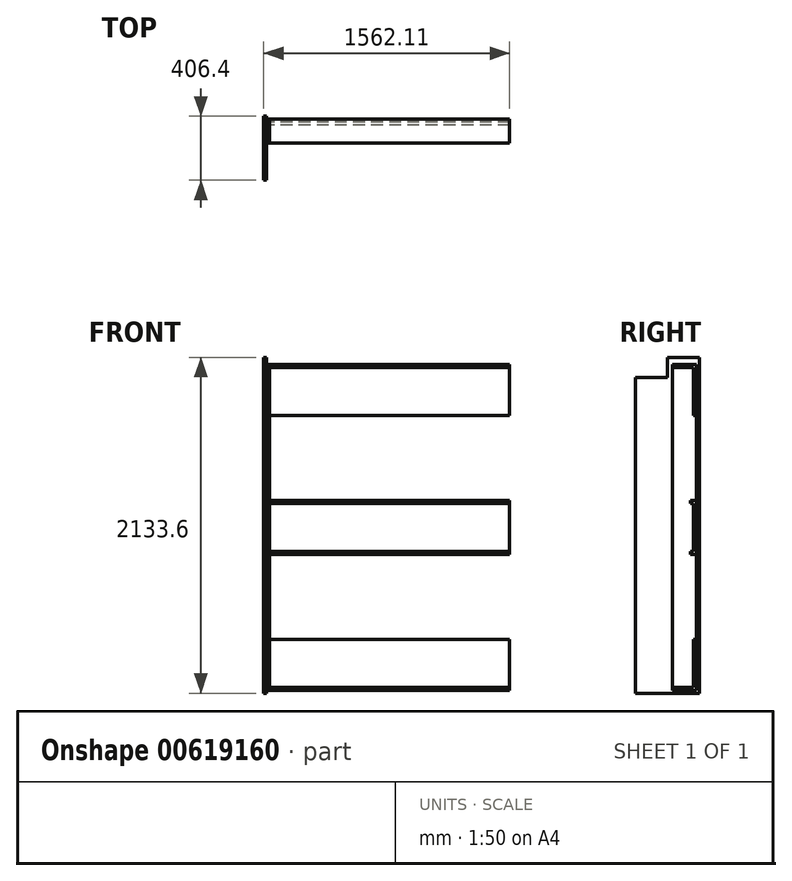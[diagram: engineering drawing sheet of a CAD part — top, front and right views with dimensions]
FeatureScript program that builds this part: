
annotation { "Feature Type Name" : "Feature", "Feature Type Description" : "" }
export const myFeature = defineFeature(function(context is Context, id is Id, definition is map)
    precondition{}
    {
        {
            var Q0;
            Q0=qCreatedBy(makeId("Right.planeOp"),FACE);
            var sketch = newSketch(context, id + "F0", { "sketchPlane" : qUnion([Q0])});
            skLineSegment(sketch, "E0.bottom", {"start": v(0, 0) * mm, "end": v(-406.4, 0) * mm});
            skLineSegment(sketch, "E0.top", {"start": v(0, 2133.6) * mm, "end": v(-203.2, 2133.6) * mm});
            skLineSegment(sketch, "E0.left", {"start": v(0, 0) * mm, "end": v(0, 2133.6) * mm});
            skLineSegment(sketch, "E0.right", {"start": v(-406.4, 0) * mm, "end": v(-406.4, 2006.6) * mm});
            skLineSegment(sketch, "E1", {"start": v(-203.2, 2133.6) * mm, "end": v(-203.2, 2006.6) * mm});
            skLineSegment(sketch, "E2", {"start": v(-203.2, 2006.6) * mm, "end": v(-406.4, 2006.6) * mm});
            skSolve(sketch);
        }
        {
            var Q0;
            Q0=makeQuery(id+"F0.imprint","IMPRINT",FACE,{"disambiguationData":[TD([[makeQuery(id+"F0.imprint","IMPRINT",EDGE,{"derivedFrom":sQuery(id+"F0.wireOp",EDGE,"E0.bottom")}),-1.0]])]});
            extrude(context, id + "F1", {"entities" : qUnion([Q0]), "depth" : 19.05 * mm, "offsetDistance" : 25.4 * mm});
        }
        {
            var Q0;
            Q0=makeQuery(id+"F1.opExtrude","CAP_FACE",FACE,{"disambiguationData":[OSD([sQuery(id+"F0.wireOp",EDGE,"E0.bottom"),sQuery(id+"F0.wireOp",EDGE,"E0.top"),sQuery(id+"F0.wireOp",EDGE,"E0.left"),sQuery(id+"F0.wireOp",EDGE,"E0.right"),sQuery(id+"F0.wireOp",EDGE,"E1"),sQuery(id+"F0.wireOp",EDGE,"E2")])],"isStart":false});
            cPlane(context, id + "F2", {"entities" : qUnion([Q0]), "cplaneType" : CPlaneType.OFFSET, "offset" : 3 / 406.4 * mm, "width" : 152.4 * mm, "height" : 152.4 * mm});
        }
        {
            var Q0;
            Q0=qCreatedBy(id+"F2.planeOp",FACE);
            var sketch = newSketch(context, id + "F3", { "sketchPlane" : qUnion([Q0])});
            skLineSegment(sketch, "E3.bottom", {"start": v(-19.05, 38.1) * mm, "end": v(-171.45, 38.1) * mm});
            skLineSegment(sketch, "E3.top", {"start": v(-19.05, 2070.1) * mm, "end": v(-171.45, 2070.1) * mm});
            skLineSegment(sketch, "E3.left", {"start": v(-19.05, 38.1) * mm, "end": v(-19.05, 2070.1) * mm});
            skLineSegment(sketch, "E3.right", {"start": v(-171.45, 38.1) * mm, "end": v(-171.45, 2070.1) * mm});
            skLineSegment(sketch, "E4.top", {"start": v(-19.05, 2089.15) * mm, "end": v(-171.45, 2089.15) * mm});
            skLineSegment(sketch, "E4.left", {"start": v(-19.05, 2070.1) * mm, "end": v(-19.05, 2089.15) * mm});
            skLineSegment(sketch, "E4.right", {"start": v(-171.45, 2070.1) * mm, "end": v(-171.45, 2089.15) * mm});
            skLineSegment(sketch, "E5.top", {"start": v(-19.05, 19.05) * mm, "end": v(-171.45, 19.05) * mm});
            skLineSegment(sketch, "E5.left", {"start": v(-19.05, 38.1) * mm, "end": v(-19.05, 19.05) * mm});
            skLineSegment(sketch, "E5.right", {"start": v(-171.45, 38.1) * mm, "end": v(-171.45, 19.05) * mm});
            skSolve(sketch);
        }
        {
            var Q0;
            Q0 = qSketchRegion(id + "F3", true);
            extrude(context, id + "F4", {"entities" : qUnion([Q0]), "depth" : 19.05 * mm, "offsetDistance" : 25.4 * mm});
        }
        {
            var Q0;
            Q0=makeQuery(id+"F4.opExtrude","CAP_FACE",FACE,{"disambiguationData":[OSD([sQuery(id+"F3.wireOp",EDGE,"E3.bottom"),sQuery(id+"F3.wireOp",EDGE,"E3.top"),sQuery(id+"F3.wireOp",EDGE,"E3.left"),sQuery(id+"F3.wireOp",EDGE,"E3.right")])],"isStart":false});
            var sketch = newSketch(context, id + "F5", { "sketchPlane" : qUnion([Q0])});
            skLineSegment(sketch, "E6.bottom", {"start": v(-19.05, 2070.1) * mm, "end": v(-38.1, 2070.1) * mm});
            skLineSegment(sketch, "E6.top", {"start": v(-19.05, 1765.3) * mm, "end": v(-38.1, 1765.3) * mm});
            skLineSegment(sketch, "E6.left", {"start": v(-19.05, 2070.1) * mm, "end": v(-19.05, 1765.3) * mm});
            skLineSegment(sketch, "E6.right", {"start": v(-38.1, 2070.1) * mm, "end": v(-38.1, 1765.3) * mm});
            skLineSegment(sketch, "E7.bottom", {"start": v(-19.05, 38.1) * mm, "end": v(-38.1, 38.1) * mm});
            skLineSegment(sketch, "E7.top", {"start": v(-19.05, 342.9) * mm, "end": v(-38.1, 342.9) * mm});
            skLineSegment(sketch, "E7.left", {"start": v(-19.05, 38.1) * mm, "end": v(-19.05, 342.9) * mm});
            skLineSegment(sketch, "E7.right", {"start": v(-38.1, 38.1) * mm, "end": v(-38.1, 342.9) * mm});
            skLineSegment(sketch, "E8.bottom", {"start": v(-19.05, 1206.5) * mm, "end": v(-38.1, 1206.5) * mm});
            skLineSegment(sketch, "E8.top", {"start": v(-19.05, 901.7) * mm, "end": v(-38.1, 901.7) * mm});
            skLineSegment(sketch, "E8.left", {"start": v(-19.05, 1206.5) * mm, "end": v(-19.05, 901.7) * mm});
            skLineSegment(sketch, "E8.right", {"start": v(-38.1, 1206.5) * mm, "end": v(-38.1, 901.7) * mm});
            skPoint(sketch, "E9", {"position": v(-19.05, 1054.1) * mm});
            skLineSegment(sketch, "E10.bottom", {"start": v(-19.05, 2070.1) * mm, "end": v(-171.45, 2070.1) * mm});
            skLineSegment(sketch, "E10.top", {"start": v(-19.05, 2089.15) * mm, "end": v(-171.45, 2089.15) * mm});
            skLineSegment(sketch, "E10.left", {"start": v(-19.05, 2070.1) * mm, "end": v(-19.05, 2089.15) * mm});
            skLineSegment(sketch, "E10.right", {"start": v(-171.45, 2070.1) * mm, "end": v(-171.45, 2089.15) * mm});
            skLineSegment(sketch, "E11.bottom", {"start": v(-19.05, 38.1) * mm, "end": v(-171.45, 38.1) * mm});
            skLineSegment(sketch, "E11.top", {"start": v(-19.05, 19.05) * mm, "end": v(-171.45, 19.05) * mm});
            skLineSegment(sketch, "E11.left", {"start": v(-19.05, 38.1) * mm, "end": v(-19.05, 19.05) * mm});
            skLineSegment(sketch, "E11.right", {"start": v(-171.45, 38.1) * mm, "end": v(-171.45, 19.05) * mm});
            skLineSegment(sketch, "E12.bottom", {"start": v(-19.05, 901.7) * mm, "end": v(-57.15, 901.7) * mm});
            skLineSegment(sketch, "E12.top", {"start": v(-19.05, 882.65) * mm, "end": v(-57.15, 882.65) * mm});
            skLineSegment(sketch, "E12.left", {"start": v(-19.05, 901.7) * mm, "end": v(-19.05, 882.65) * mm});
            skLineSegment(sketch, "E12.right", {"start": v(-57.15, 901.7) * mm, "end": v(-57.15, 882.65) * mm});
            skLineSegment(sketch, "E13.bottom", {"start": v(-19.05, 1206.5) * mm, "end": v(-57.15, 1206.5) * mm});
            skLineSegment(sketch, "E13.top", {"start": v(-19.05, 1225.55) * mm, "end": v(-57.15, 1225.55) * mm});
            skLineSegment(sketch, "E13.left", {"start": v(-19.05, 1206.5) * mm, "end": v(-19.05, 1225.55) * mm});
            skLineSegment(sketch, "E13.right", {"start": v(-57.15, 1206.5) * mm, "end": v(-57.15, 1225.55) * mm});
            skSolve(sketch);
        }
        {
            var Q0;
            Q0 = qSketchRegion(id + "F5", true);
            extrude(context, id + "F6", {"entities" : qUnion([Q0]), "depth" : 1524 * mm, "offsetDistance" : 25.4 * mm});
        }
        {
            var Q0;
            Q0=makeQuery(id+"F4.opExtrude","CAP_FACE",FACE,{"disambiguationData":[OSD([sQuery(id+"F3.wireOp",EDGE,"E3.left"),sQuery(id+"F3.wireOp",EDGE,"E3.right"),sQuery(id+"F3.wireOp",EDGE,"E4.top"),sQuery(id+"F3.wireOp",EDGE,"E4.left"),sQuery(id+"F3.wireOp",EDGE,"E4.right"),sQuery(id+"F3.wireOp",EDGE,"E5.top"),sQuery(id+"F3.wireOp",EDGE,"E5.left"),sQuery(id+"F3.wireOp",EDGE,"E5.right")])],"isStart":false});
            var sketch = newSketch(context, id + "F7", { "sketchPlane" : qUnion([Q0])});
            skLineSegment(sketch, "E14.bottom", {"start": v(-88.9, 2070.1) * mm, "end": v(-101.6, 2070.1) * mm});
            skLineSegment(sketch, "E14.top", {"start": v(-88.9, 2019.3) * mm, "end": v(-101.6, 2019.3) * mm});
            skLineSegment(sketch, "E14.left", {"start": v(-88.9, 2070.1) * mm, "end": v(-88.9, 2019.3) * mm});
            skLineSegment(sketch, "E14.right", {"start": v(-101.6, 2070.1) * mm, "end": v(-101.6, 2019.3) * mm});
            skLineSegment(sketch, "E15.0.1.0", {"start": v(-88.9, 1915.03) * mm, "end": v(-101.6, 1915.03) * mm});
            skLineSegment(sketch, "E15.0.1.1", {"start": v(-101.6, 1965.83) * mm, "end": v(-101.6, 1915.03) * mm});
            skLineSegment(sketch, "E15.0.1.2", {"start": v(-88.9, 1965.83) * mm, "end": v(-88.9, 1915.03) * mm});
            skLineSegment(sketch, "E15.0.1.3", {"start": v(-88.9, 1965.83) * mm, "end": v(-101.6, 1965.83) * mm});
            skLineSegment(sketch, "E15.0.2.0", {"start": v(-88.9, 1810.75) * mm, "end": v(-101.6, 1810.75) * mm});
            skLineSegment(sketch, "E15.0.2.1", {"start": v(-101.6, 1861.55) * mm, "end": v(-101.6, 1810.75) * mm});
            skLineSegment(sketch, "E15.0.2.2", {"start": v(-88.9, 1861.55) * mm, "end": v(-88.9, 1810.75) * mm});
            skLineSegment(sketch, "E15.0.2.3", {"start": v(-88.9, 1861.55) * mm, "end": v(-101.6, 1861.55) * mm});
            skLineSegment(sketch, "E15.0.3.0", {"start": v(-88.9, 1706.48) * mm, "end": v(-101.6, 1706.48) * mm});
            skLineSegment(sketch, "E15.0.3.1", {"start": v(-101.6, 1757.28) * mm, "end": v(-101.6, 1706.48) * mm});
            skLineSegment(sketch, "E15.0.3.2", {"start": v(-88.9, 1757.28) * mm, "end": v(-88.9, 1706.48) * mm});
            skLineSegment(sketch, "E15.0.3.3", {"start": v(-88.9, 1757.28) * mm, "end": v(-101.6, 1757.28) * mm});
            skLineSegment(sketch, "E15.0.4.0", {"start": v(-88.9, 1602.2) * mm, "end": v(-101.6, 1602.2) * mm});
            skLineSegment(sketch, "E15.0.4.1", {"start": v(-101.6, 1653) * mm, "end": v(-101.6, 1602.2) * mm});
            skLineSegment(sketch, "E15.0.4.2", {"start": v(-88.9, 1653) * mm, "end": v(-88.9, 1602.2) * mm});
            skLineSegment(sketch, "E15.0.4.3", {"start": v(-88.9, 1653) * mm, "end": v(-101.6, 1653) * mm});
            skLineSegment(sketch, "E15.0.5.0", {"start": v(-88.9, 1497.93) * mm, "end": v(-101.6, 1497.93) * mm});
            skLineSegment(sketch, "E15.0.5.1", {"start": v(-101.6, 1548.73) * mm, "end": v(-101.6, 1497.93) * mm});
            skLineSegment(sketch, "E15.0.5.2", {"start": v(-88.9, 1548.73) * mm, "end": v(-88.9, 1497.93) * mm});
            skLineSegment(sketch, "E15.0.5.3", {"start": v(-88.9, 1548.73) * mm, "end": v(-101.6, 1548.73) * mm});
            skLineSegment(sketch, "E15.0.6.0", {"start": v(-88.9, 1393.66) * mm, "end": v(-101.6, 1393.66) * mm});
            skLineSegment(sketch, "E15.0.6.1", {"start": v(-101.6, 1444.46) * mm, "end": v(-101.6, 1393.66) * mm});
            skLineSegment(sketch, "E15.0.6.2", {"start": v(-88.9, 1444.46) * mm, "end": v(-88.9, 1393.66) * mm});
            skLineSegment(sketch, "E15.0.6.3", {"start": v(-88.9, 1444.46) * mm, "end": v(-101.6, 1444.46) * mm});
            skLineSegment(sketch, "E15.0.7.0", {"start": v(-88.9, 1289.38) * mm, "end": v(-101.6, 1289.38) * mm});
            skLineSegment(sketch, "E15.0.7.1", {"start": v(-101.6, 1340.18) * mm, "end": v(-101.6, 1289.38) * mm});
            skLineSegment(sketch, "E15.0.7.2", {"start": v(-88.9, 1340.18) * mm, "end": v(-88.9, 1289.38) * mm});
            skLineSegment(sketch, "E15.0.7.3", {"start": v(-88.9, 1340.18) * mm, "end": v(-101.6, 1340.18) * mm});
            skLineSegment(sketch, "E15.0.8.0", {"start": v(-88.9, 1185.11) * mm, "end": v(-101.6, 1185.11) * mm});
            skLineSegment(sketch, "E15.0.8.1", {"start": v(-101.6, 1235.91) * mm, "end": v(-101.6, 1185.11) * mm});
            skLineSegment(sketch, "E15.0.8.2", {"start": v(-88.9, 1235.91) * mm, "end": v(-88.9, 1185.11) * mm});
            skLineSegment(sketch, "E15.0.8.3", {"start": v(-88.9, 1235.91) * mm, "end": v(-101.6, 1235.91) * mm});
            skLineSegment(sketch, "E15.0.9.0", {"start": v(-88.9, 1080.84) * mm, "end": v(-101.6, 1080.84) * mm});
            skLineSegment(sketch, "E15.0.9.1", {"start": v(-101.6, 1131.64) * mm, "end": v(-101.6, 1080.84) * mm});
            skLineSegment(sketch, "E15.0.9.2", {"start": v(-88.9, 1131.64) * mm, "end": v(-88.9, 1080.84) * mm});
            skLineSegment(sketch, "E15.0.9.3", {"start": v(-88.9, 1131.64) * mm, "end": v(-101.6, 1131.64) * mm});
            skLineSegment(sketch, "E15.0.10.0", {"start": v(-88.9, 976.56) * mm, "end": v(-101.6, 976.56) * mm});
            skLineSegment(sketch, "E15.0.10.1", {"start": v(-101.6, 1027.36) * mm, "end": v(-101.6, 976.56) * mm});
            skLineSegment(sketch, "E15.0.10.2", {"start": v(-88.9, 1027.36) * mm, "end": v(-88.9, 976.56) * mm});
            skLineSegment(sketch, "E15.0.10.3", {"start": v(-88.9, 1027.36) * mm, "end": v(-101.6, 1027.36) * mm});
            skLineSegment(sketch, "E15.0.11.0", {"start": v(-88.9, 872.29) * mm, "end": v(-101.6, 872.29) * mm});
            skLineSegment(sketch, "E15.0.11.1", {"start": v(-101.6, 923.09) * mm, "end": v(-101.6, 872.29) * mm});
            skLineSegment(sketch, "E15.0.11.2", {"start": v(-88.9, 923.09) * mm, "end": v(-88.9, 872.29) * mm});
            skLineSegment(sketch, "E15.0.11.3", {"start": v(-88.9, 923.09) * mm, "end": v(-101.6, 923.09) * mm});
            skLineSegment(sketch, "E15.0.12.0", {"start": v(-88.9, 768.02) * mm, "end": v(-101.6, 768.02) * mm});
            skLineSegment(sketch, "E15.0.12.1", {"start": v(-101.6, 818.82) * mm, "end": v(-101.6, 768.02) * mm});
            skLineSegment(sketch, "E15.0.12.2", {"start": v(-88.9, 818.82) * mm, "end": v(-88.9, 768.02) * mm});
            skLineSegment(sketch, "E15.0.12.3", {"start": v(-88.9, 818.82) * mm, "end": v(-101.6, 818.82) * mm});
            skLineSegment(sketch, "E15.0.13.0", {"start": v(-88.9, 663.74) * mm, "end": v(-101.6, 663.74) * mm});
            skLineSegment(sketch, "E15.0.13.1", {"start": v(-101.6, 714.54) * mm, "end": v(-101.6, 663.74) * mm});
            skLineSegment(sketch, "E15.0.13.2", {"start": v(-88.9, 714.54) * mm, "end": v(-88.9, 663.74) * mm});
            skLineSegment(sketch, "E15.0.13.3", {"start": v(-88.9, 714.54) * mm, "end": v(-101.6, 714.54) * mm});
            skLineSegment(sketch, "E15.0.14.0", {"start": v(-88.9, 559.47) * mm, "end": v(-101.6, 559.47) * mm});
            skLineSegment(sketch, "E15.0.14.1", {"start": v(-101.6, 610.27) * mm, "end": v(-101.6, 559.47) * mm});
            skLineSegment(sketch, "E15.0.14.2", {"start": v(-88.9, 610.27) * mm, "end": v(-88.9, 559.47) * mm});
            skLineSegment(sketch, "E15.0.14.3", {"start": v(-88.9, 610.27) * mm, "end": v(-101.6, 610.27) * mm});
            skLineSegment(sketch, "E15.0.15.0", {"start": v(-88.9, 455.2) * mm, "end": v(-101.6, 455.2) * mm});
            skLineSegment(sketch, "E15.0.15.1", {"start": v(-101.6, 506) * mm, "end": v(-101.6, 455.2) * mm});
            skLineSegment(sketch, "E15.0.15.2", {"start": v(-88.9, 506) * mm, "end": v(-88.9, 455.2) * mm});
            skLineSegment(sketch, "E15.0.15.3", {"start": v(-88.9, 506) * mm, "end": v(-101.6, 506) * mm});
            skLineSegment(sketch, "E15.0.16.0", {"start": v(-88.9, 350.92) * mm, "end": v(-101.6, 350.92) * mm});
            skLineSegment(sketch, "E15.0.16.1", {"start": v(-101.6, 401.72) * mm, "end": v(-101.6, 350.92) * mm});
            skLineSegment(sketch, "E15.0.16.2", {"start": v(-88.9, 401.72) * mm, "end": v(-88.9, 350.92) * mm});
            skLineSegment(sketch, "E15.0.16.3", {"start": v(-88.9, 401.72) * mm, "end": v(-101.6, 401.72) * mm});
            skLineSegment(sketch, "E15.0.17.0", {"start": v(-88.9, 246.65) * mm, "end": v(-101.6, 246.65) * mm});
            skLineSegment(sketch, "E15.0.17.1", {"start": v(-101.6, 297.45) * mm, "end": v(-101.6, 246.65) * mm});
            skLineSegment(sketch, "E15.0.17.2", {"start": v(-88.9, 297.45) * mm, "end": v(-88.9, 246.65) * mm});
            skLineSegment(sketch, "E15.0.17.3", {"start": v(-88.9, 297.45) * mm, "end": v(-101.6, 297.45) * mm});
            skLineSegment(sketch, "E15.0.18.0", {"start": v(-88.9, 142.37) * mm, "end": v(-101.6, 142.37) * mm});
            skLineSegment(sketch, "E15.0.18.1", {"start": v(-101.6, 193.17) * mm, "end": v(-101.6, 142.37) * mm});
            skLineSegment(sketch, "E15.0.18.2", {"start": v(-88.9, 193.17) * mm, "end": v(-88.9, 142.37) * mm});
            skLineSegment(sketch, "E15.0.18.3", {"start": v(-88.9, 193.17) * mm, "end": v(-101.6, 193.17) * mm});
            skLineSegment(sketch, "E15.0.19.0", {"start": v(-88.9, 38.1) * mm, "end": v(-101.6, 38.1) * mm});
            skLineSegment(sketch, "E15.0.19.1", {"start": v(-101.6, 88.9) * mm, "end": v(-101.6, 38.1) * mm});
            skLineSegment(sketch, "E15.0.19.2", {"start": v(-88.9, 88.9) * mm, "end": v(-88.9, 38.1) * mm});
            skLineSegment(sketch, "E15.0.19.3", {"start": v(-88.9, 88.9) * mm, "end": v(-101.6, 88.9) * mm});
            skLineSegment(sketch, "E15.direction1", {"start": v(-101.6, 2019.3) * mm, "end": v(-127, 2019.3) * mm, "construction": true});
            skLineSegment(sketch, "E15.direction2", {"start": v(-101.6, 2019.3) * mm, "end": v(-101.6, 1915.03) * mm, "construction": true});
            skSolve(sketch);
        }
        {
            var Q0;
            Q0=sQuery(id+"F7.wireOp",EDGE,"E15.0.19.0");
            var Q1;
            Q1=sQuery(id+"F7.wireOp",EDGE,"E15.0.19.2");
            var Q2;
            Q2=sQuery(id+"F7.wireOp",EDGE,"E15.0.19.3");
            var Q3;
            Q3=sQuery(id+"F7.wireOp",EDGE,"E15.0.19.1");
            var Q4;
            Q4=sQuery(id+"F7.wireOp",EDGE,"E15.0.7.0");
            var Q5;
            Q5=sQuery(id+"F7.wireOp",EDGE,"E15.0.7.2");
            var Q6;
            Q6=sQuery(id+"F7.wireOp",EDGE,"E15.0.9.1");
            var Q7;
            Q7=sQuery(id+"F7.wireOp",EDGE,"E15.0.5.1");
            var Q8;
            Q8=sQuery(id+"F7.wireOp",EDGE,"E15.0.9.2");
            var Q9;
            Q9=sQuery(id+"F7.wireOp",EDGE,"E15.0.5.2");
            var Q10;
            Q10=sQuery(id+"F7.wireOp",EDGE,"E14.left");
            var Q11;
            Q11=sQuery(id+"F7.wireOp",EDGE,"E14.right");
            var Q12;
            Q12=sQuery(id+"F7.wireOp",EDGE,"E15.0.1.2");
            var Q13;
            Q13=sQuery(id+"F7.wireOp",EDGE,"E15.0.14.1");
            var Q14;
            Q14=sQuery(id+"F7.wireOp",EDGE,"E15.0.14.2");
            var Q15;
            Q15=sQuery(id+"F7.wireOp",EDGE,"E15.0.18.2");
            var Q16;
            Q16=sQuery(id+"F7.wireOp",EDGE,"E15.0.12.2");
            var Q17;
            Q17=sQuery(id+"F7.wireOp",EDGE,"E15.0.10.2");
            var Q18;
            Q18=sQuery(id+"F7.wireOp",EDGE,"E15.0.6.1");
            var Q19;
            Q19=sQuery(id+"F7.wireOp",EDGE,"E15.0.8.2");
            var Q20;
            Q20=sQuery(id+"F7.wireOp",EDGE,"E15.0.6.2");
            var Q21;
            Q21=sQuery(id+"F7.wireOp",EDGE,"E15.0.16.2");
            var Q22;
            Q22=sQuery(id+"F7.wireOp",EDGE,"E15.0.18.1");
            var Q23;
            Q23=sQuery(id+"F7.wireOp",EDGE,"E15.0.10.1");
            var Q24;
            Q24=sQuery(id+"F7.wireOp",EDGE,"E15.0.8.3");
            var Q25;
            Q25=sQuery(id+"F7.wireOp",EDGE,"E15.0.6.3");
            var Q26;
            Q26=sQuery(id+"F7.wireOp",EDGE,"E15.0.7.1");
            var Q27;
            Q27=sQuery(id+"F7.wireOp",EDGE,"E15.0.5.0");
            var Q28;
            Q28=sQuery(id+"F7.wireOp",EDGE,"E15.0.11.2");
            var Q29;
            Q29=sQuery(id+"F7.wireOp",EDGE,"E15.0.13.1");
            var Q30;
            Q30=sQuery(id+"F7.wireOp",EDGE,"E15.0.5.3");
            var Q31;
            Q31=sQuery(id+"F7.wireOp",EDGE,"E15.0.17.1");
            var Q32;
            Q32=sQuery(id+"F7.wireOp",EDGE,"E15.0.15.2");
            var Q33;
            Q33=sQuery(id+"F7.wireOp",EDGE,"E15.0.9.3");
            var Q34;
            Q34=sQuery(id+"F7.wireOp",EDGE,"E15.0.13.2");
            var Q35;
            Q35=sQuery(id+"F7.wireOp",EDGE,"E15.0.11.3");
            var Q36;
            Q36=sQuery(id+"F7.wireOp",EDGE,"E15.0.7.3");
            var Q37;
            Q37=sQuery(id+"F7.wireOp",EDGE,"E15.0.15.3");
            var Q38;
            Q38=sQuery(id+"F7.wireOp",EDGE,"E15.0.12.1");
            var Q39;
            Q39=sQuery(id+"F7.wireOp",EDGE,"E15.0.17.2");
            var Q40;
            Q40=sQuery(id+"F7.wireOp",EDGE,"E15.0.3.2");
            var Q41;
            Q41=sQuery(id+"F7.wireOp",EDGE,"E15.0.3.3");
            var Q42;
            Q42=sQuery(id+"F7.wireOp",EDGE,"E14.bottom");
            var Q43;
            Q43=sQuery(id+"F7.wireOp",EDGE,"E15.0.8.1");
            var Q44;
            Q44=sQuery(id+"F7.wireOp",EDGE,"E15.0.1.0");
            var Q45;
            Q45=sQuery(id+"F7.wireOp",EDGE,"E15.0.1.1");
            var Q46;
            Q46=sQuery(id+"F7.wireOp",EDGE,"E15.0.2.1");
            var Q47;
            Q47=sQuery(id+"F7.wireOp",EDGE,"E15.0.2.2");
            var Q48;
            Q48=sQuery(id+"F7.wireOp",EDGE,"E15.0.16.1");
            var Q49;
            Q49=sQuery(id+"F7.wireOp",EDGE,"E15.0.2.3");
            var Q50;
            Q50=sQuery(id+"F7.wireOp",EDGE,"E15.0.3.0");
            var Q51;
            Q51=sQuery(id+"F7.wireOp",EDGE,"E15.0.10.0");
            var Q52;
            Q52=sQuery(id+"F7.wireOp",EDGE,"E15.0.4.2");
            var Q53;
            Q53=sQuery(id+"F7.wireOp",EDGE,"E15.0.12.3");
            var Q54;
            Q54=sQuery(id+"F7.wireOp",EDGE,"E15.0.4.3");
            var Q55;
            Q55=sQuery(id+"F7.wireOp",EDGE,"E15.0.12.0");
            var Q56;
            Q56=sQuery(id+"F7.wireOp",EDGE,"E15.0.16.3");
            var Q57;
            Q57=sQuery(id+"F7.wireOp",EDGE,"E15.0.8.0");
            var Q58;
            Q58=sQuery(id+"F7.wireOp",EDGE,"E15.0.18.3");
            var Q59;
            Q59=sQuery(id+"F7.wireOp",EDGE,"E15.0.14.3");
            var Q60;
            Q60=sQuery(id+"F7.wireOp",EDGE,"E15.0.13.0");
            var Q61;
            Q61=sQuery(id+"F7.wireOp",EDGE,"E15.0.11.1");
            var Q62;
            Q62=sQuery(id+"F7.wireOp",EDGE,"E15.0.9.0");
            var Q63;
            Q63=sQuery(id+"F7.wireOp",EDGE,"E15.0.16.0");
            var Q64;
            Q64=sQuery(id+"F7.wireOp",EDGE,"E15.0.17.0");
            var Q65;
            Q65=sQuery(id+"F7.wireOp",EDGE,"E15.0.15.1");
            var Q66;
            Q66=sQuery(id+"F7.wireOp",EDGE,"E15.0.15.0");
            var Q67;
            Q67=sQuery(id+"F7.wireOp",EDGE,"E15.0.11.0");
            var Q68;
            Q68=sQuery(id+"F7.wireOp",EDGE,"E15.0.17.3");
            var Q69;
            Q69=sQuery(id+"F7.wireOp",EDGE,"E15.0.13.3");
            var Q70;
            Q70=sQuery(id+"F7.wireOp",EDGE,"E15.0.3.1");
            var Q71;
            Q71=sQuery(id+"F7.wireOp",EDGE,"E15.0.4.1");
            var Q72;
            Q72=sQuery(id+"F7.wireOp",EDGE,"E14.top");
            var Q73;
            Q73=sQuery(id+"F7.wireOp",EDGE,"E15.0.1.3");
            var Q74;
            Q74=sQuery(id+"F7.wireOp",EDGE,"E15.0.2.0");
            var Q75;
            Q75=sQuery(id+"F7.wireOp",EDGE,"E15.0.6.0");
            var Q76;
            Q76=sQuery(id+"F7.wireOp",EDGE,"E15.0.18.0");
            var Q77;
            Q77=sQuery(id+"F7.wireOp",EDGE,"E15.0.14.0");
            var Q78;
            Q78=sQuery(id+"F7.wireOp",EDGE,"E15.0.4.0");
            var Q79;
            Q79=sQuery(id+"F7.wireOp",EDGE,"E15.0.10.3");
            var Q80;
            Q80=makeQuery(id+"F6.opExtrude","CAP_FACE",FACE,{"disambiguationData":[OSD([sQuery(id+"F5.wireOp",EDGE,"E7.top"),sQuery(id+"F5.wireOp",EDGE,"E7.left"),sQuery(id+"F5.wireOp",EDGE,"E7.right"),sQuery(id+"F5.wireOp",EDGE,"E11.bottom"),sQuery(id+"F5.wireOp",EDGE,"E11.top"),sQuery(id+"F5.wireOp",EDGE,"E11.left"),sQuery(id+"F5.wireOp",EDGE,"E11.right")])],"isStart":false});
            extrude(context, id + "F8", {"bodyType" : ToolBodyType.SURFACE, "surfaceEntities" : qUnion([Q0, Q1, Q2, Q3, Q4, Q5, Q6, Q7, Q8, Q9, Q10, Q11, Q12, Q13, Q14, Q15, Q16, Q17, Q18, Q19, Q20, Q21, Q22, Q23, Q24, Q25, Q26, Q27, Q28, Q29, Q30, Q31, Q32, Q33, Q34, Q35, Q36, Q37, Q38, Q39, Q40, Q41, Q42, Q43, Q44, Q45, Q46, Q47, Q48, Q49, Q50, Q51, Q52, Q53, Q54, Q55, Q56, Q57, Q58, Q59, Q60, Q61, Q62, Q63, Q64, Q65, Q66, Q67, Q68, Q69, Q70, Q71, Q72, Q73, Q74, Q75, Q76, Q77, Q78, Q79]), "endBound" : BoundingType.UP_TO_SURFACE, "depth" : 25.4 * mm, "endBoundEntityFace" : qUnion([Q80]), "offsetDistance" : 25.4 * mm});
        }
    });
